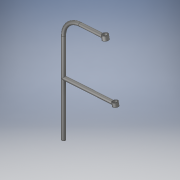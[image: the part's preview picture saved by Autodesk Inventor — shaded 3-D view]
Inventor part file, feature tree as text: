
AUTODESK INVENTOR PART (.ipt)
format: ipt  version: 2018 (Build 220112000, 112)  size: 158,720 bytes
history: native  units: in
note: dims shown in document units (in); Inventor stores cm internally (conversion verified against a paired STEP export)
features: sketch x8, extrude x3, sweep x2, plane x2
ambient origin geometry x8: Origin, YZ Plane, XZ Plane, XY Plane, X Axis, Y Axis, Z Axis, Center Point
bodies: Solid1 (feature_tree)
feature tree (15):
  sweep  "Sweep1"
  sweep  "Sweep2"
  sketch  "Sketch5"  dims[d17=21.5in d18=5.0in]
  plane  "Work Plane1"
  plane  "Work Plane2"
  extrude  "Extrusion1"  Depth=15.0in
  extrude  "Extrusion3"  Depth=15.0in
  extrude  "Extrusion2"  Depth=5.0in
  sketch  "Sketch1"  dims[d1=1.0in d4=0.0in d5=0.0in]
  sketch  "Sketch2"  dims[d6=1.0in d7=0.0in d8=0.0in]
  sketch  "Sketch3"  dims[d13=15.0in d14=19.5in]
  sketch  "Sketch4"  dims[d15=14.5in d16=15.0in]
  sketch  "Sketch6"  dims[d19=14.5in]
  sketch  "Sketch7"  dims[d20=15.0in]
  sketch  "Sketch8"  dims[d21=26.25in d22=1.58in d23=1.15in d24=0.0in d25=1.13in d26=1.0in d27=0.0in d28=1.433in d29=1.027in d30=0.0in d31=20.0in d32=0.0in]
